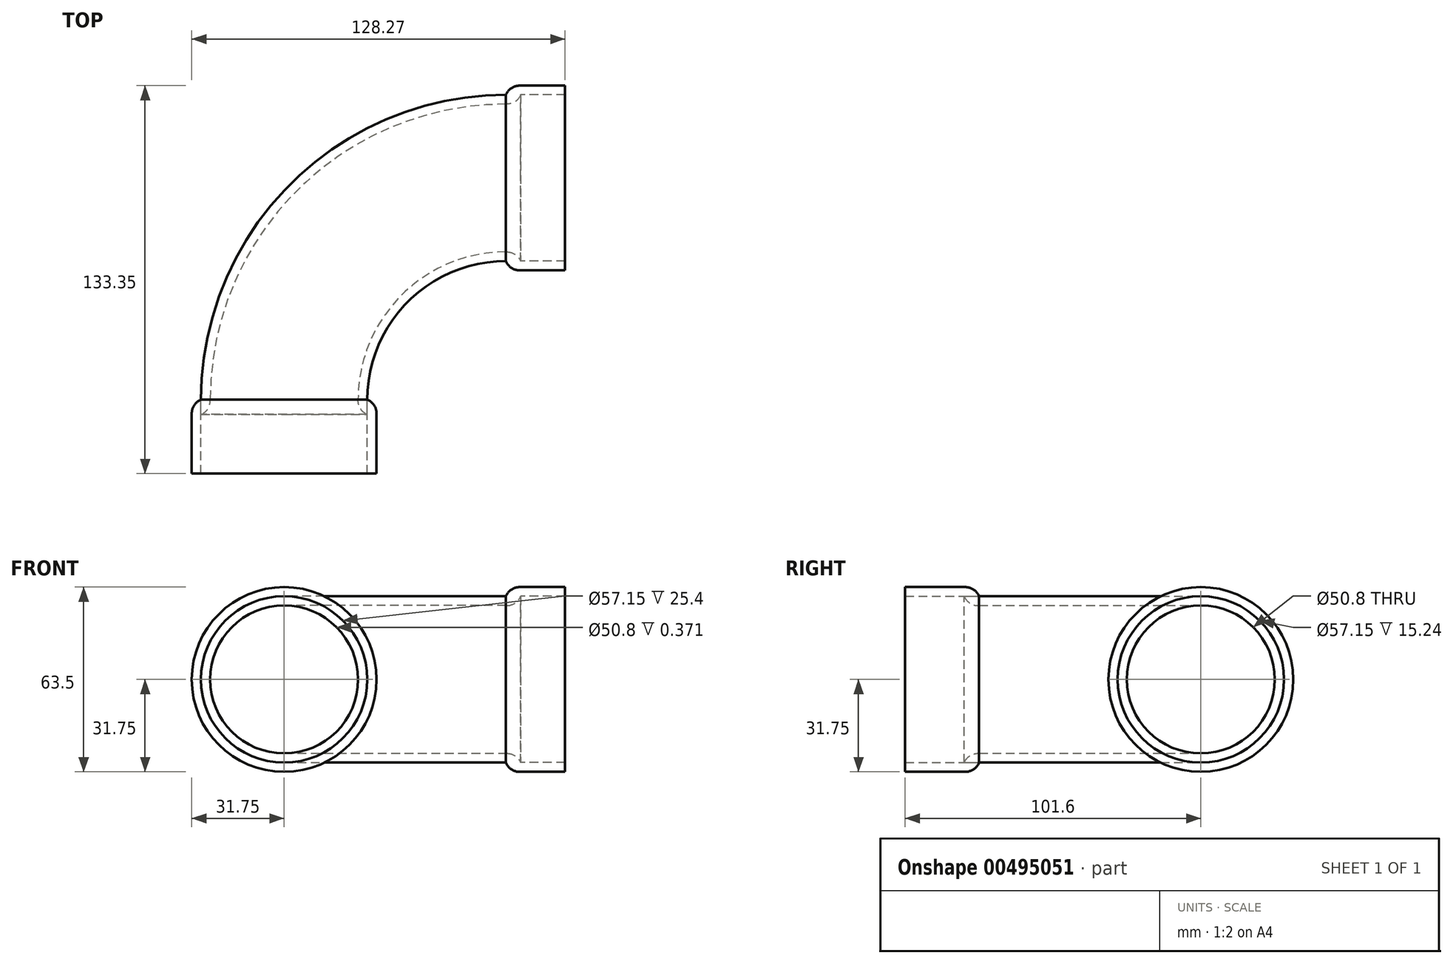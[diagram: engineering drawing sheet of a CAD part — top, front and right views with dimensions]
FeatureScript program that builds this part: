
annotation { "Feature Type Name" : "Feature", "Feature Type Description" : "" }
export const myFeature = defineFeature(function(context is Context, id is Id, definition is map)
    precondition{}
    {
        {
            var Q0;
            Q0=qCreatedBy(makeId("Front.planeOp"),FACE);
            var sketch = newSketch(context, id + "F0", { "sketchPlane" : qUnion([Q0])});
            skCircle(sketch, "E0", {"center": v(0, 0) * mm, "radius": 25.4 * mm});
            skCircle(sketch, "E1", {"center": v(0, 0) * mm, "radius": 28.58 * mm});
            skCircle(sketch, "E2", {"center": v(0, 0) * mm, "radius": 31.75 * mm});
            skSolve(sketch);
        }
        {
            var Q0;
            Q0=qCreatedBy(makeId("Top.planeOp"),FACE);
            var sketch = newSketch(context, id + "F1", { "sketchPlane" : qUnion([Q0])});
            skLineSegment(sketch, "E3", {"start": v(0, 0) * mm, "end": v(0, 0) * mm});
            skLineSegment(sketch, "E4", {"start": v(76.2, 76.2) * mm, "end": v(76.2, 76.2) * mm});
            skPoint(sketch, "E5.visualSharp", {"position": v(0, 76.2) * mm});
            skArc(sketch, "E5.filletArc", {"start": v(76.2, 76.2) * mm, "mid": v(22.32, 53.88) * mm, "end": v(0, 0) * mm});
            skSolve(sketch);
        }
        {
            var Q0;
            Q0=makeQuery(id+"F0.imprint","IMPRINT",FACE,{"disambiguationData":[TD([[makeQuery(id+"F0.imprint","IMPRINT",EDGE,{"derivedFrom":sQuery(id+"F0.wireOp",EDGE,"E0")}),-1.0]])]});
            var Q1;
            Q1=sQuery(id+"F1.wireOp",EDGE,"E5.filletArc");
            sweep(context, id + "F2", {"profiles" : qUnion([Q0]), "path" : qUnion([Q1])});
        }
        {
            var Q0;
            Q0=makeQuery(id+"F0.imprint","IMPRINT",FACE,{"disambiguationData":[TD([[makeQuery(id+"F0.imprint","IMPRINT",EDGE,{"derivedFrom":sQuery(id+"F0.wireOp",EDGE,"E1")}),-1.0]])]});
            extrude(context, id + "F3", {"entities" : qUnion([Q0]), "depth" : 25.4 * mm});
        }
        {
            var Q0;
            Q0=makeQuery(id+"F0.imprint","IMPRINT",FACE,{"disambiguationData":[TD([[makeQuery(id+"F0.imprint","IMPRINT",EDGE,{"derivedFrom":sQuery(id+"F0.wireOp",EDGE,"E0")}),-1.0]])]});
            extrude(context, id + "F4", {"entities" : qUnion([Q0]), "depth" : 5.08 * mm});
        }
        {
            var Q0;
            Q0=makeQuery(id+"F2.opSweep","CAP_FACE",FACE,{"disambiguationData":[OSD([sQuery(id+"F0.wireOp",EDGE,"E0"),sQuery(id+"F0.wireOp",EDGE,"E1"),sQuery(id+"F1.wireOp",VERTEX,"E5.filletArc.start")])],"isStart":false});
            var sketch = newSketch(context, id + "F5", { "sketchPlane" : qUnion([Q0])});
            skCircle(sketch, "E6.0", {"center": v(76.2, 0) * mm, "radius": 25.4 * mm});
            skCircle(sketch, "E7.0", {"center": v(76.2, 0) * mm, "radius": 28.58 * mm});
            skCircle(sketch, "E8", {"center": v(76.2, 0) * mm, "radius": 31.75 * mm});
            skSolve(sketch);
        }
        {
            var Q0;
            Q0=makeQuery(id+"F5.imprint","IMPRINT",FACE,{"disambiguationData":[TD([[makeQuery(id+"F5.imprint","IMPRINT",EDGE,{"derivedFrom":sQuery(id+"F5.wireOp",EDGE,"E6.0")}),1.0]])]});
            extrude(context, id + "F6", {"entities" : qUnion([Q0]), "operationType" : NewBodyOperationType.ADD, "depth" : 5.08 * mm});
        }
        {
            var Q0;
            Q0=makeQuery(id+"F5.imprint","IMPRINT",FACE,{"disambiguationData":[TD([[makeQuery(id+"F5.imprint","IMPRINT",EDGE,{"derivedFrom":sQuery(id+"F5.wireOp",EDGE,"E7.0")}),-1.0]])]});
            extrude(context, id + "F7", {"entities" : qUnion([Q0]), "operationType" : NewBodyOperationType.ADD, "depth" : 20.32 * mm});
        }
        {
            var Q0;
            Q0=makeQuery(id+"F6.opExtrude","CAP_EDGE",EDGE,{"disambiguationData":[OSD([sQuery(id+"F5.wireOp",EDGE,"E6.0")])],"isStart":false});
            var Q1;
            Q1=makeQuery(id+"F7.opExtrude","CAP_EDGE",EDGE,{"disambiguationData":[OSD([sQuery(id+"F5.wireOp",EDGE,"E8")])],"isStart":true});
            var Q2;
            Q2=makeQuery(id+"F4.opExtrude","CAP_EDGE",EDGE,{"disambiguationData":[OSD([sQuery(id+"F0.wireOp",EDGE,"E0")])],"isStart":false});
            var Q3;
            Q3=makeQuery(id+"F3.opExtrude","CAP_EDGE",EDGE,{"disambiguationData":[OSD([sQuery(id+"F0.wireOp",EDGE,"E2")])],"isStart":true});
            fillet(context, id + "F8", {"entities" : qUnion([Q0, Q1, Q2, Q3]), "radius" : 5.08 * mm, "tangentPropagation" : true, "allowEdgeOverflow" : false});
        }
    });
